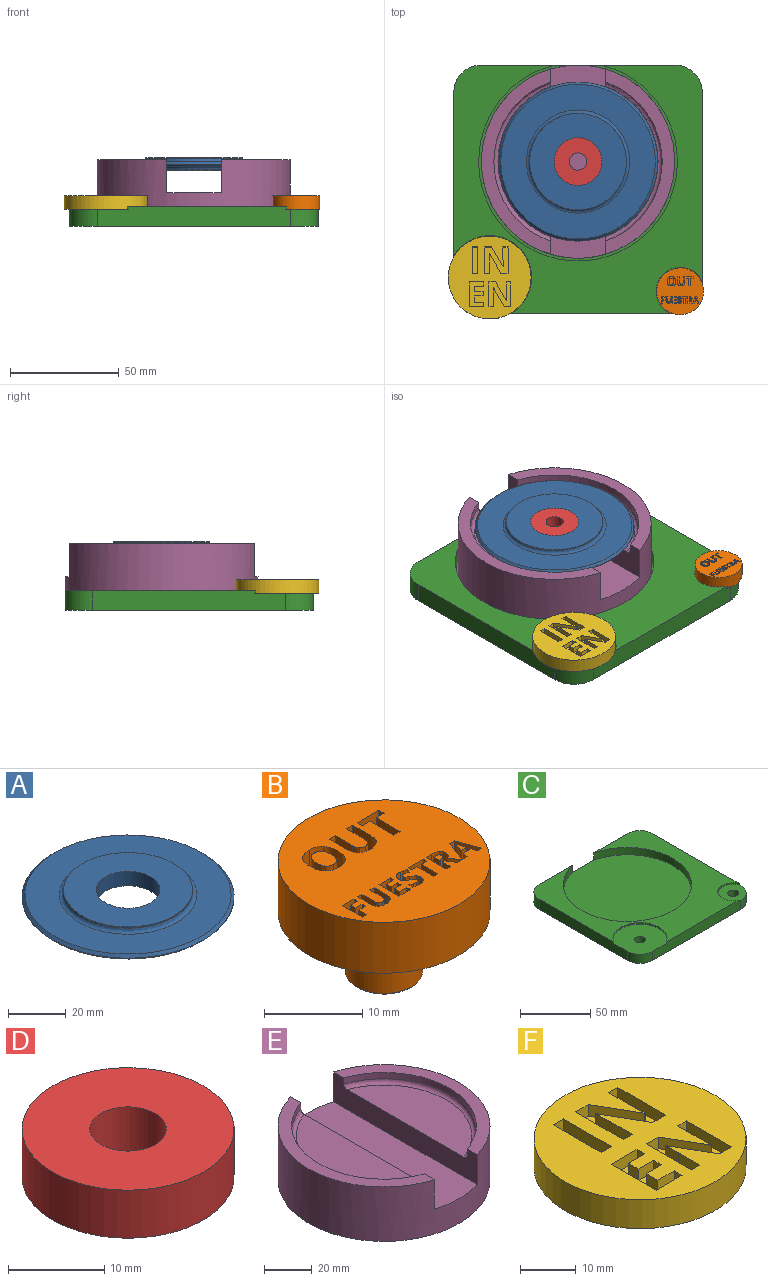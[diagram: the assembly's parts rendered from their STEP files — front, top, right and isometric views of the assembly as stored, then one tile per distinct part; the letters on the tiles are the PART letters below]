
ASSEMBLY  parts=6 mates=5
PART A: 12 faces, bbox 73.2x73.2x7.3 mm
  f0: plane 44.45x44.45mm, normal (0,0,-1), area 1172.2mm2, adj f1,f7
  f1: cylinder r=10.99mm len=21.98mm, axis (0,0,1), area 421mm2, adj f0,f2
  f2: plane 44.45x44.45mm, normal (0,0,1), area 1172.2mm2, adj f1,f3
  f3: cylinder r=22.23mm len=44.45mm, axis (0,0,1), area 64.7mm2, adj f2,f10
  f4: plane 71.12x71.12mm, normal (0,0,1), area 2200.7mm2, adj f9,f10
  f5: cylinder r=36.58mm len=73.15mm, axis (0,0,1), area 20.4mm2, adj f8,f9
  f6: plane 71.12x71.12mm, normal (0,0,-1), area 2200.7mm2, adj f8,f11
  f7: cylinder r=22.23mm len=44.45mm, axis (0,0,1), area 64.7mm2, adj f0,f11
  f8: cone r=36.58mm half-angle=45deg, axis (0,0,1), area 325.6mm2, adj f5,f6
  f9: cone r=35.56mm half-angle=45deg, axis (0,0,-1), area 325.6mm2, adj f4,f5
  f10: torus R=23.75mm, axis (0,0,-1), area 342.6mm2, adj f3,f4
  f11: torus R=23.75mm, axis (0,0,1), area 342.6mm2, adj f6,f7
PART B: 160 faces, bbox 21.6x21.6x14 mm
  f0: plane 21.59x21.59mm, normal (0,0,1), area 314.7mm2, adj f1,f9,f10,f11,f12,f13,f14,f15
  f1: cylinder r=10.79mm len=21.59mm, axis (0,0,-1), area 430.7mm2, adj f0,f2
  f2: plane 21.59x21.59mm, normal (0,0,-1), area 317.4mm2, adj f1,f3
  f3: cylinder r=3.94mm len=7.87mm, axis (0,0,1), area 182.2mm2, adj f2,f5
  f4: plane 7.37x7.37mm, normal (0,0,-1), area 42.6mm2, adj f5
  f5: cone r=3.68mm half-angle=45deg, axis (0,0,1), area 8.6mm2, adj f3,f4
  f6: extruded ~2.54x1.05mm, area 2.8mm2, adj f7,f17,f18,f158
  f7: plane 2.54x0.75mm, normal (0,-1,0), area 1.9mm2, adj f6,f8,f18,f158
  f8: extruded ~2.54x1.24mm, area 3.3mm2, adj f7,f17,f18,f158
  f9: plane 2.54x0.68mm, normal (0.96,0.29,0), area 1.8mm2, adj f0,f10,f16,f18
  f10: plane 2.54x0.65mm, normal (0,1,0), area 1.7mm2, adj f0,f9,f11,f18
  f11: plane 2.88x2.54mm, normal (-0.94,-0.33,0), area 7.7mm2, adj f0,f10,f12,f18
  f12: plane 2.54x0.74mm, normal (0,-1,0), area 1.9mm2, adj f0,f11,f13,f18
  f13: plane 2.88x2.54mm, normal (0.94,-0.33,0), area 7.7mm2, adj f0,f12,f14,f18
  f14: plane 2.54x0.65mm, normal (0,1,0), area 1.7mm2, adj f0,f13,f15,f18
  f15: plane 2.54x0.68mm, normal (-0.96,0.29,0), area 1.8mm2, adj f0,f14,f16,f18
  f16: plane 2.54x1.04mm, normal (0,1,0), area 2.7mm2, adj f0,f9,f15,f18
  f17: extruded ~2.54x0.19mm, area 0.5mm2, adj f6,f8,f18,f158
  f18: plane 2.88x2.77mm, normal (0,0,1), area 3.7mm2, adj f6,f7,f8,f9,f10,f11,f12,f13
  f19: plane 2.54x1.1mm, normal (-1,0,0), area 2.8mm2, adj f0,f20,f37,f38
  f20: plane 2.54x0.32mm, normal (0,1,0), area 0.8mm2, adj f0,f19,f21,f38
  f21: plane 2.54x1.1mm, normal (0.85,0.53,0), area 3.3mm2, adj f0,f20,f22,f38
  f22: plane 2.54x0.67mm, normal (0,1,0), area 1.7mm2, adj f0,f21,f23,f38
  f23: extruded ~2.54x1.25mm, area 3.8mm2, adj f0,f22,f24,f38
  f24: extruded ~2.54x0.39mm, area 1.3mm2, adj f0,f23,f25,f38
  f25: extruded ~2.54x0.45mm, area 1.2mm2, adj f0,f24,f26,f38
  f26: extruded ~2.54x0.65mm, area 1.9mm2, adj f0,f25,f27,f38
  f27: extruded ~2.54x0.86mm, area 2.3mm2, adj f0,f26,f28,f38
  f28: plane 2.54x0.83mm, normal (0,-1,0), area 2.1mm2, adj f0,f27,f29,f38
  f29: plane 2.86x2.54mm, normal (1,0,0), area 7.3mm2, adj f0,f28,f37,f38
  f30: plane 2.54x0.2mm, normal (0,-1,0), area 0.5mm2, adj f31,f36,f38,f39
  f31: plane 2.54x0.77mm, normal (-1,0,0), area 2mm2, adj f30,f32,f38,f39
  f32: plane 2.54x0.18mm, normal (0,1,0), area 0.5mm2, adj f31,f33,f38,f39
  f33: extruded ~2.54x0.43mm, area 1.1mm2, adj f32,f34,f38,f39
  f34: extruded ~2.54x0.29mm, area 0.9mm2, adj f33,f35,f38,f39
  f35: extruded ~2.54x0.3mm, area 0.9mm2, adj f34,f36,f38,f39
  f36: extruded ~2.54x0.43mm, area 1.1mm2, adj f30,f35,f38,f39
  f37: plane 2.54x0.61mm, normal (0,1,0), area 1.5mm2, adj f0,f19,f29,f38
  f38: plane 2.86x2.29mm, normal (0,0,1), area 4mm2, adj f19,f20,f21,f22,f23,f24,f25,f26
  f39: plane 0.77x0.76mm, normal (0,0,1), area 0.5mm2, adj f30,f31,f32,f33,f34,f35,f36
  f40: plane 2.54x0.88mm, normal (0,1,0), area 2.2mm2, adj f0,f41,f47,f48
  f41: plane 3.43x2.54mm, normal (-1,0,0), area 8.7mm2, adj f0,f40,f42,f48
  f42: plane 2.54x1.13mm, normal (0,1,0), area 2.9mm2, adj f0,f41,f43,f48
  f43: plane 2.54x0.74mm, normal (-1,0,0), area 1.9mm2, adj f0,f42,f44,f48
  f44: plane 3.15x2.54mm, normal (0,-1,0), area 8mm2, adj f0,f43,f45,f48
  f45: plane 2.54x0.74mm, normal (1,0,0), area 1.9mm2, adj f0,f44,f46,f48
  f46: plane 2.54x1.13mm, normal (0,1,0), area 2.9mm2, adj f0,f45,f47,f48
  f47: plane 3.43x2.54mm, normal (1,0,0), area 8.7mm2, adj f0,f40,f46,f48
  f48: plane 4.17x3.15mm, normal (0,0,1), area 5.3mm2, adj f40,f41,f42,f43,f44,f45,f46,f47
  f49: plane 2.7x2.54mm, normal (-1,0,0), area 6.8mm2, adj f0,f50,f63,f64
  f50: plane 2.54x0.88mm, normal (0,-1,0), area 2.2mm2, adj f0,f49,f51,f64
  f51: plane 2.55x2.54mm, normal (1,0,0), area 6.5mm2, adj f0,f50,f52,f64
  f52: extruded ~2.54x0.71mm, area 1.9mm2, adj f0,f51,f53,f64
  f53: extruded ~2.54x0.63mm, area 1.8mm2, adj f0,f52,f54,f64
  f54: extruded ~2.54x0.64mm, area 1.8mm2, adj f0,f53,f55,f64
  f55: extruded ~2.54x0.71mm, area 1.9mm2, adj f0,f54,f56,f64
  f56: plane 2.55x2.54mm, normal (-1,0,0), area 6.5mm2, adj f0,f55,f57,f64
  f57: plane 2.54x0.88mm, normal (0,-1,0), area 2.2mm2, adj f0,f56,f58,f64
  f58: plane 2.69x2.54mm, normal (1,0,0), area 6.8mm2, adj f0,f57,f59,f64
  f59: extruded ~2.54x1.13mm, area 3.2mm2, adj f0,f58,f60,f64
  f60: extruded ~2.54x1.25mm, area 3.4mm2, adj f0,f59,f61,f64
  f61: extruded ~2.54x0.92mm, area 2.4mm2, adj f0,f60,f62,f64
  f62: extruded ~2.54x0.6mm, area 2.1mm2, adj f0,f61,f63,f64
  f63: extruded ~2.54x0.81mm, area 2.1mm2, adj f0,f49,f62,f64
  f64: plane 4.22x3.42mm, normal (0,0,1), area 7.9mm2, adj f49,f50,f51,f52,f53,f54,f55,f56
  f65: plane 2.54x0.61mm, normal (0,1,0), area 1.5mm2, adj f0,f66,f72,f73
  f66: plane 2.54x2.36mm, normal (-1,0,0), area 6mm2, adj f0,f65,f67,f73
  f67: plane 2.54x0.78mm, normal (0,1,0), area 2mm2, adj f0,f66,f68,f73
  f68: plane 2.54x0.51mm, normal (-1,0,0), area 1.3mm2, adj f0,f67,f69,f73
  f69: plane 2.54x2.16mm, normal (0,-1,0), area 5.5mm2, adj f0,f68,f70,f73
  f70: plane 2.54x0.51mm, normal (1,0,0), area 1.3mm2, adj f0,f69,f71,f73
  f71: plane 2.54x0.78mm, normal (0,1,0), area 2mm2, adj f0,f70,f72,f73
  f72: plane 2.54x2.36mm, normal (1,0,0), area 6mm2, adj f0,f65,f71,f73
  f73: plane 2.86x2.16mm, normal (0,0,1), area 2.5mm2, adj f65,f66,f67,f68,f69,f70,f71,f72
  f74: extruded ~2.54x0.61mm, area 1.8mm2, adj f0,f75,f101,f102
  f75: extruded ~2.54x0.47mm, area 1.3mm2, adj f0,f74,f76,f102
  f76: extruded ~2.54x0.55mm, area 1.7mm2, adj f0,f75,f77,f102
  f77: extruded ~2.54x0.38mm, area 1.1mm2, adj f0,f76,f78,f102
  f78: extruded ~2.54x0.12mm, area 0.4mm2, adj f0,f77,f79,f102
  f79: extruded ~2.54x0.14mm, area 0.4mm2, adj f0,f78,f80,f102
  f80: extruded ~2.54x0.21mm, area 0.6mm2, adj f0,f79,f81,f102
  f81: extruded ~2.54x0.26mm, area 0.7mm2, adj f0,f80,f82,f102
  f82: extruded ~2.54x0.29mm, area 0.8mm2, adj f0,f81,f83,f102
  f83: extruded ~2.54x0.38mm, area 1mm2, adj f0,f82,f84,f102
  f84: plane 2.54x0.47mm, normal (-0.92,0.38,0), area 1.3mm2, adj f0,f83,f85,f102
  f85: extruded ~2.54x0.42mm, area 1.1mm2, adj f0,f84,f86,f102
  f86: extruded ~2.54x0.43mm, area 1.1mm2, adj f0,f85,f87,f102
  f87: extruded ~2.54x0.71mm, area 1.9mm2, adj f0,f86,f88,f102
  f88: extruded ~2.54x0.6mm, area 1.7mm2, adj f0,f87,f89,f102
  f89: extruded ~2.54x0.35mm, area 0.9mm2, adj f0,f88,f90,f102
  f90: extruded ~2.54x0.26mm, area 0.9mm2, adj f0,f89,f91,f102
  f91: extruded ~2.54x0.39mm, area 1.2mm2, adj f0,f90,f92,f102
  f92: extruded ~2.54x0.37mm, area 1.1mm2, adj f0,f91,f93,f102
  f93: extruded ~2.54x0.14mm, area 0.5mm2, adj f0,f92,f94,f102
  f94: extruded ~2.54x0.15mm, area 0.4mm2, adj f0,f93,f95,f102
  f95: extruded ~2.54x0.23mm, area 0.7mm2, adj f0,f94,f96,f102
  f96: extruded ~2.54x0.31mm, area 0.8mm2, adj f0,f95,f97,f102
  f97: extruded ~2.54x0.37mm, area 0.9mm2, adj f0,f96,f98,f102
  f98: extruded ~2.54x0.49mm, area 1.3mm2, adj f0,f97,f99,f102
  f99: plane 2.54x0.56mm, normal (1,0,0), area 1.4mm2, adj f0,f98,f100,f102
  f100: extruded ~2.54x0.81mm, area 2.1mm2, adj f0,f99,f101,f102
  f101: extruded ~2.54x0.78mm, area 2.1mm2, adj f0,f74,f100,f102
  f102: plane 2.95x1.87mm, normal (0,0,1), area 3.1mm2, adj f74,f75,f76,f77,f78,f79,f80,f81
  f103: plane 2.54x1.65mm, normal (0,1,0), area 4.2mm2, adj f0,f104,f114,f115
  f104: plane 2.54x0.5mm, normal (-1,0,0), area 1.3mm2, adj f0,f103,f105,f115
  f105: plane 2.54x1.04mm, normal (0,-1,0), area 2.6mm2, adj f0,f104,f106,f115
  f106: plane 2.54x0.74mm, normal (-1,0,0), area 1.9mm2, adj f0,f105,f107,f115
  f107: plane 2.54x0.97mm, normal (0,1,0), area 2.5mm2, adj f0,f106,f108,f115
  f108: plane 2.54x0.5mm, normal (-1,0,0), area 1.3mm2, adj f0,f107,f109,f115
  f109: plane 2.54x0.97mm, normal (0,-1,0), area 2.5mm2, adj f0,f108,f110,f115
  f110: plane 2.54x0.63mm, normal (-1,0,0), area 1.6mm2, adj f0,f109,f111,f115
  f111: plane 2.54x1.04mm, normal (0,1,0), area 2.6mm2, adj f0,f110,f112,f115
  f112: plane 2.54x0.5mm, normal (-1,0,0), area 1.3mm2, adj f0,f111,f113,f115
  f113: plane 2.54x1.65mm, normal (0,-1,0), area 4.2mm2, adj f0,f112,f114,f115
  f114: plane 2.86x2.54mm, normal (1,0,0), area 7.3mm2, adj f0,f103,f113,f115
  f115: plane 2.86x1.65mm, normal (0,0,1), area 3.3mm2, adj f103,f104,f105,f106,f107,f108,f109,f110
  f116: plane 2.54x1.85mm, normal (-1,0,0), area 4.7mm2, adj f0,f117,f130,f131
  f117: plane 2.54x0.61mm, normal (0,-1,0), area 1.5mm2, adj f0,f116,f118,f131
  f118: plane 2.54x1.75mm, normal (1,0,0), area 4.4mm2, adj f0,f117,f119,f131
  f119: extruded ~2.54x0.49mm, area 1.3mm2, adj f0,f118,f120,f131
  f120: extruded ~2.54x0.43mm, area 1.2mm2, adj f0,f119,f121,f131
  f121: extruded ~2.54x0.44mm, area 1.2mm2, adj f0,f120,f122,f131
  f122: extruded ~2.54x0.49mm, area 1.3mm2, adj f0,f121,f123,f131
  f123: plane 2.54x1.75mm, normal (-1,0,0), area 4.5mm2, adj f0,f122,f124,f131
  f124: plane 2.54x0.61mm, normal (0,-1,0), area 1.5mm2, adj f0,f123,f125,f131
  f125: plane 2.54x1.85mm, normal (1,0,0), area 4.7mm2, adj f0,f124,f126,f131
  f126: extruded ~2.54x0.78mm, area 2.2mm2, adj f0,f125,f127,f131
  f127: extruded ~2.54x0.86mm, area 2.4mm2, adj f0,f126,f128,f131
  f128: extruded ~2.54x0.64mm, area 1.7mm2, adj f0,f127,f129,f131
  f129: extruded ~2.54x0.41mm, area 1.4mm2, adj f0,f128,f130,f131
  f130: extruded ~2.54x0.56mm, area 1.5mm2, adj f0,f116,f129,f131
  f131: plane 2.9x2.35mm, normal (0,0,1), area 3.8mm2, adj f116,f117,f118,f119,f120,f121,f122,f123
  f132: extruded ~2.54x1.05mm, area 2.8mm2, adj f133,f145,f146,f159
  f133: extruded ~2.54x1.05mm, area 2.8mm2, adj f132,f134,f146,f159
  f134: extruded ~2.54x0.8mm, area 2.3mm2, adj f133,f135,f146,f159
  f135: extruded ~2.54x1.41mm, area 5.1mm2, adj f134,f136,f146,f159
  f136: extruded ~2.54x1.41mm, area 5.1mm2, adj f135,f145,f146,f159
  f137: extruded ~2.54x1.59mm, area 4.3mm2, adj f0,f138,f144,f146
  f138: extruded ~2.54x1.59mm, area 4.3mm2, adj f0,f137,f139,f146
  f139: extruded ~2.54x1.47mm, area 4.1mm2, adj f0,f138,f140,f146
  f140: extruded ~2.54x1.47mm, area 4.1mm2, adj f0,f139,f141,f146
  f141: extruded ~2.54x1.59mm, area 4.3mm2, adj f0,f140,f142,f146
  f142: extruded ~2.54x1.6mm, area 4.4mm2, adj f0,f141,f143,f146
  f143: extruded ~2.54x1.47mm, area 4.1mm2, adj f0,f142,f144,f146
  f144: extruded ~2.54x1.47mm, area 4.1mm2, adj f0,f137,f143,f146
  f145: extruded ~2.54x0.79mm, area 2.3mm2, adj f132,f136,f146,f159
  f146: plane 4.29x3.97mm, normal (0,0,1), area 9.1mm2, adj f132,f133,f134,f135,f136,f137,f138,f139
  f147: plane 2.54x0.6mm, normal (0,1,0), area 1.5mm2, adj f0,f148,f156,f157
  f148: plane 2.54x1.13mm, normal (-1,0,0), area 2.9mm2, adj f0,f147,f149,f157
  f149: plane 2.54x0.97mm, normal (0,1,0), area 2.5mm2, adj f0,f148,f150,f157
  f150: plane 2.54x0.5mm, normal (-1,0,0), area 1.3mm2, adj f0,f149,f151,f157
  f151: plane 2.54x0.97mm, normal (0,-1,0), area 2.5mm2, adj f0,f150,f152,f157
  f152: plane 2.54x0.74mm, normal (-1,0,0), area 1.9mm2, adj f0,f151,f153,f157
  f153: plane 2.54x1.04mm, normal (0,1,0), area 2.7mm2, adj f0,f152,f154,f157
  f154: plane 2.54x0.5mm, normal (-1,0,0), area 1.3mm2, adj f0,f153,f155,f157
  f155: plane 2.54x1.64mm, normal (0,-1,0), area 4.2mm2, adj f0,f154,f156,f157
  f156: plane 2.86x2.54mm, normal (1,0,0), area 7.3mm2, adj f0,f147,f155,f157
  f157: plane 2.86x1.64mm, normal (0,0,1), area 2.7mm2, adj f147,f148,f149,f150,f151,f152,f153,f154
  f158: plane 1.24x0.75mm, normal (0,0,1), area 0.5mm2, adj f6,f7,f8,f17
  f159: plane 2.81x2.11mm, normal (0,0,1), area 5mm2, adj f132,f133,f134,f135,f136,f145
PART C: 18 faces, bbox 114.3x114.3x9.1 mm
  f0: plane 21.21x21.21mm, normal (0,0,1), area 302.4mm2, adj f4,f5,f9,f11,f15
  f1: plane 35.81x35.81mm, normal (0,0,1), area 1029.5mm2, adj f2,f5,f8,f12,f16
  f2: plane 88.9x9.14mm, normal (-1,0,0), area 795.4mm2, adj f1,f6,f8,f10,f13,f16
  f3: plane 88.9x9.14mm, normal (0,1,0), area 677mm2, adj f6,f7,f10,f13,f14,f17
  f4: plane 88.9x9.14mm, normal (1,0,0), area 810.6mm2, adj f0,f6,f9,f10,f14,f15
  f5: plane 88.9x9.14mm, normal (0,-1,0), area 793.1mm2, adj f0,f1,f6,f8,f9,f10,f15,f16
  f6: plane 114.3x114.3mm, normal (0,0,-1), area 12828.6mm2, adj f2,f3,f4,f5,f11,f12,f13,f14
  f7: cylinder r=45.72mm len=91.44mm, axis (0,0,-1), area 1687mm2, adj f3,f10,f17
  f8: cylinder r=19.3mm len=35.81mm, axis (0,0,-1), area 88.8mm2, adj f1,f2,f5,f10
  f9: cylinder r=11.05mm len=21.21mm, axis (0,0,-1), area 54.8mm2, adj f0,f4,f5,f10
  f10: plane 114.3x114.3mm, normal (0,0,1), area 4948.1mm2, adj f2,f3,f4,f5,f7,f8,f9,f13
  f11: cylinder r=3.94mm len=7.87mm, axis (0,0,1), area 194.8mm2, adj f0,f6
  f12: cylinder r=3.94mm len=7.87mm, axis (0,0,1), area 194.8mm2, adj f1,f6
  f13: cylinder r=12.7mm len=12.7mm, axis (0,0,1), area 182.4mm2, adj f2,f3,f6,f10
  f14: cylinder r=12.7mm len=12.7mm, axis (0,0,-1), area 182.4mm2, adj f3,f4,f6,f10
  f15: cylinder r=12.7mm len=12.7mm, axis (0,0,1), area 157.1mm2, adj f0,f4,f5,f6
  f16: cylinder r=12.7mm len=12.7mm, axis (0,0,-1), area 157.1mm2, adj f1,f2,f5,f6
  f17: plane 91.44x90.17mm, normal (0,0,1), area 6548.8mm2, adj f3,f7
PART D: 4 faces, bbox 22x22x6.1 mm
  f0: plane 22x22mm, normal (0,0,-1), area 330.5mm2, adj f2,f3
  f1: plane 22x22mm, normal (0,0,1), area 330.5mm2, adj f2,f3
  f2: cylinder r=3.97mm len=7.94mm, axis (0,0,1), area 152mm2, adj f0,f1
  f3: cylinder r=11mm len=22mm, axis (0,0,1), area 421.3mm2, adj f0,f1
PART E: 13 faces, bbox 88.9x88.9x27.9 mm
  f0: cylinder r=38.73mm len=73.19mm, axis (0,0,-1), area 304.2mm2, adj f4,f6,f10
  f1: cylinder r=44.45mm len=88.9mm, axis (0,0,-1), area 7018.2mm2, adj f2,f6,f8,f10,f11,f12
  f2: plane 85.19x31.75mm, normal (0,0,1), area 599.2mm2, adj f1,f5,f11
  f3: plane 69.14x24.13mm, normal (0,0,1), area 1214.1mm2, adj f4,f10
  f4: torus R=36.83mm, axis (0,0,-1), area 280.1mm2, adj f0,f3,f10
  f5: cylinder r=38.73mm len=73.19mm, axis (0,0,-1), area 304.2mm2, adj f2,f9,f11
  f6: plane 85.19x31.75mm, normal (0,0,1), area 599.2mm2, adj f0,f1,f10
  f7: plane 69.14x24.13mm, normal (0,0,1), area 1214.1mm2, adj f9,f11
  f8: plane 88.9x88.9mm, normal (0,0,-1), area 6207.2mm2, adj f1
  f9: torus R=36.83mm, axis (0,0,-1), area 280.1mm2, adj f5,f7,f11
  f10: plane 85.19x15.24mm, normal (-1,0,0), area 928.2mm2, adj f0,f1,f3,f4,f6,f12
  f11: plane 85.19x15.24mm, normal (1,0,0), area 928.2mm2, adj f1,f2,f5,f7,f9,f12
  f12: plane 88.9x25.4mm, normal (0,0,1), area 2227mm2, adj f1,f10,f11
PART F: 54 faces, bbox 38.1x38.1x14 mm
  f0: plane 38.1x38.1mm, normal (0,0,1), area 899mm2, adj f5,f6,f7,f8,f9,f11,f12,f13
  f1: plane 38.1x38.1mm, normal (0,0,-1), area 1091.4mm2, adj f2,f5
  f2: cylinder r=3.94mm len=7.87mm, axis (0,0,1), area 182.2mm2, adj f1,f4
  f3: plane 7.37x7.37mm, normal (0,0,-1), area 42.6mm2, adj f4
  f4: cone r=3.68mm half-angle=45deg, axis (0,0,1), area 8.6mm2, adj f2,f3
  f5: cylinder r=19.05mm len=38.1mm, axis (0,0,1), area 760.1mm2, adj f0,f1
  f6: plane 12.15x2.54mm, normal (1,0,0), area 30.9mm2, adj f0,f7,f9,f10
  f7: plane 2.58x2.54mm, normal (0,1,0), area 6.5mm2, adj f0,f6,f8,f10
  f8: plane 12.15x2.54mm, normal (-1,0,0), area 30.9mm2, adj f0,f7,f9,f10
  f9: plane 2.58x2.54mm, normal (0,-1,0), area 6.5mm2, adj f0,f6,f8,f10
  f10: plane 12.15x2.58mm, normal (0,0,1), area 31.3mm2, adj f6,f7,f8,f9
  f11: plane 3.08x2.54mm, normal (0,1,0), area 7.8mm2, adj f0,f12,f24,f25
  f12: plane 11.43x2.54mm, normal (-1,0,0), area 29mm2, adj f0,f11,f13,f25
  f13: plane 2.54x2.18mm, normal (0,-1,0), area 5.5mm2, adj f0,f12,f14,f25
  f14: plane 5.41x2.54mm, normal (1,0,0), area 13.7mm2, adj f0,f13,f15,f25
  f15: extruded ~3.15x2.54mm, area 8mm2, adj f0,f14,f16,f25
  f16: plane 2.54x0.06mm, normal (0,-1,0), area 0.1mm2, adj f0,f15,f17,f25
  f17: plane 8.56x4.97mm, normal (-0.87,-0.5,0), area 25.1mm2, adj f0,f16,f18,f25
  f18: plane 3.06x2.54mm, normal (0,-1,0), area 7.8mm2, adj f0,f17,f19,f25
  f19: plane 11.43x2.54mm, normal (1,0,0), area 29mm2, adj f0,f18,f20,f25
  f20: plane 2.54x2.17mm, normal (0,1,0), area 5.5mm2, adj f0,f19,f21,f25
  f21: plane 5.38x2.54mm, normal (-1,0,0), area 13.7mm2, adj f0,f20,f22,f25
  f22: extruded ~3.27x2.54mm, area 8.3mm2, adj f0,f21,f23,f25
  f23: plane 2.54x0.07mm, normal (0,1,0), area 0.2mm2, adj f0,f22,f24,f25
  f24: plane 8.65x4.98mm, normal (0.87,0.5,0), area 25.3mm2, adj f0,f11,f23,f25
  f25: plane 11.43x10.14mm, normal (0,0,1), area 74.1mm2, adj f11,f12,f13,f14,f15,f16,f17,f18
  f26: plane 6.58x2.54mm, normal (0,1,0), area 16.7mm2, adj f0,f27,f37,f38
  f27: plane 2.54x2mm, normal (-1,0,0), area 5.1mm2, adj f0,f26,f28,f38
  f28: plane 4.16x2.54mm, normal (0,-1,0), area 10.6mm2, adj f0,f27,f29,f38
  f29: plane 2.95x2.54mm, normal (-1,0,0), area 7.5mm2, adj f0,f28,f30,f38
  f30: plane 3.87x2.54mm, normal (0,1,0), area 9.8mm2, adj f0,f29,f31,f38
  f31: plane 2.54x1.99mm, normal (-1,0,0), area 5mm2, adj f0,f30,f32,f38
  f32: plane 3.87x2.54mm, normal (0,-1,0), area 9.8mm2, adj f0,f31,f33,f38
  f33: plane 2.54x2.51mm, normal (-1,0,0), area 6.4mm2, adj f0,f32,f34,f38
  f34: plane 4.16x2.54mm, normal (0,1,0), area 10.6mm2, adj f0,f33,f35,f38
  f35: plane 2.54x1.99mm, normal (-1,0,0), area 5mm2, adj f0,f34,f36,f38
  f36: plane 6.58x2.54mm, normal (0,-1,0), area 16.7mm2, adj f0,f35,f37,f38
  f37: plane 11.43x2.54mm, normal (1,0,0), area 29mm2, adj f0,f26,f36,f38
  f38: plane 11.43x6.58mm, normal (0,0,1), area 52mm2, adj f26,f27,f28,f29,f30,f31,f32,f33
  f39: plane 3.27x2.54mm, normal (0,1,0), area 8.3mm2, adj f0,f40,f52,f53
  f40: plane 12.15x2.54mm, normal (-1,0,0), area 30.9mm2, adj f0,f39,f41,f53
  f41: plane 2.54x2.32mm, normal (0,-1,0), area 5.9mm2, adj f0,f40,f42,f53
  f42: plane 5.75x2.54mm, normal (1,0,0), area 14.6mm2, adj f0,f41,f43,f53
  f43: extruded ~3.35x2.54mm, area 8.5mm2, adj f0,f42,f44,f53
  f44: plane 2.54x0.06mm, normal (0,-1,0), area 0.1mm2, adj f0,f43,f45,f53
  f45: plane 9.1x5.28mm, normal (-0.87,-0.5,0), area 26.7mm2, adj f0,f44,f46,f53
  f46: plane 3.25x2.54mm, normal (0,-1,0), area 8.3mm2, adj f0,f45,f47,f53
  f47: plane 12.15x2.54mm, normal (1,0,0), area 30.9mm2, adj f0,f46,f48,f53
  f48: plane 2.54x2.3mm, normal (0,1,0), area 5.9mm2, adj f0,f47,f49,f53
  f49: plane 5.72x2.54mm, normal (-1,0,0), area 14.5mm2, adj f0,f48,f50,f53
  f50: extruded ~3.47x2.54mm, area 8.8mm2, adj f0,f49,f51,f53
  f51: plane 2.54x0.07mm, normal (0,1,0), area 0.2mm2, adj f0,f50,f52,f53
  f52: plane 9.19x5.29mm, normal (0.87,0.5,0), area 26.9mm2, adj f0,f39,f51,f53
  f53: plane 12.15x10.78mm, normal (0,0,1), area 83.7mm2, adj f39,f40,f41,f42,f43,f44,f45,f46
PLACE A t=(0,0,-5.08)mm
PLACE B t=(46.99,-59.69,-28.96)mm
PLACE C at identity
PLACE D t=(0,0,-5.08)mm
PLACE E t=(0,0,-5.08)mm
PLACE F t=(-40.64,-53.34,-28.96)mm
MATE fastened F.f2 <-> C.f8  axis (0,0,-1) through (-40.64,-53.34,-22.86)mm
MATE fastened D.f2 <-> A.f1  axis (0,0,1) through (0,0,1.02)mm
MATE fastened D.f3 <-> E.f0  axis (0,0,-1) through (0,0,-5.08)mm
MATE fastened E.f1 <-> C.f7  axis (0,0,-1) through (0,0,-27.94)mm
MATE fastened B.f3 <-> C.f9  axis (0,0,-1) through (46.99,-59.69,-22.86)mm
